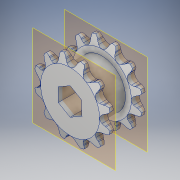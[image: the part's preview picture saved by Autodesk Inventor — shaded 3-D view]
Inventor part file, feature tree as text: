
AUTODESK INVENTOR PART (.ipt)
format: ipt  version: 2017 (Build 210142000, 142)  size: 599,040 bytes
history: native  units: in
note: dims shown in document units (in); Inventor stores cm internally (conversion verified against a paired STEP export)
features: plane x2, other x1
ambient origin geometry x8: Origin, YZ Plane, XZ Plane, XY Plane, X Axis, Y Axis, Z Axis, Center Point
bodies: Solid1 (feature_tree)
feature tree (3):
  plane  "Work Plane1"
  plane  "Work Plane2"
  other  "Cut-Extrude3"
